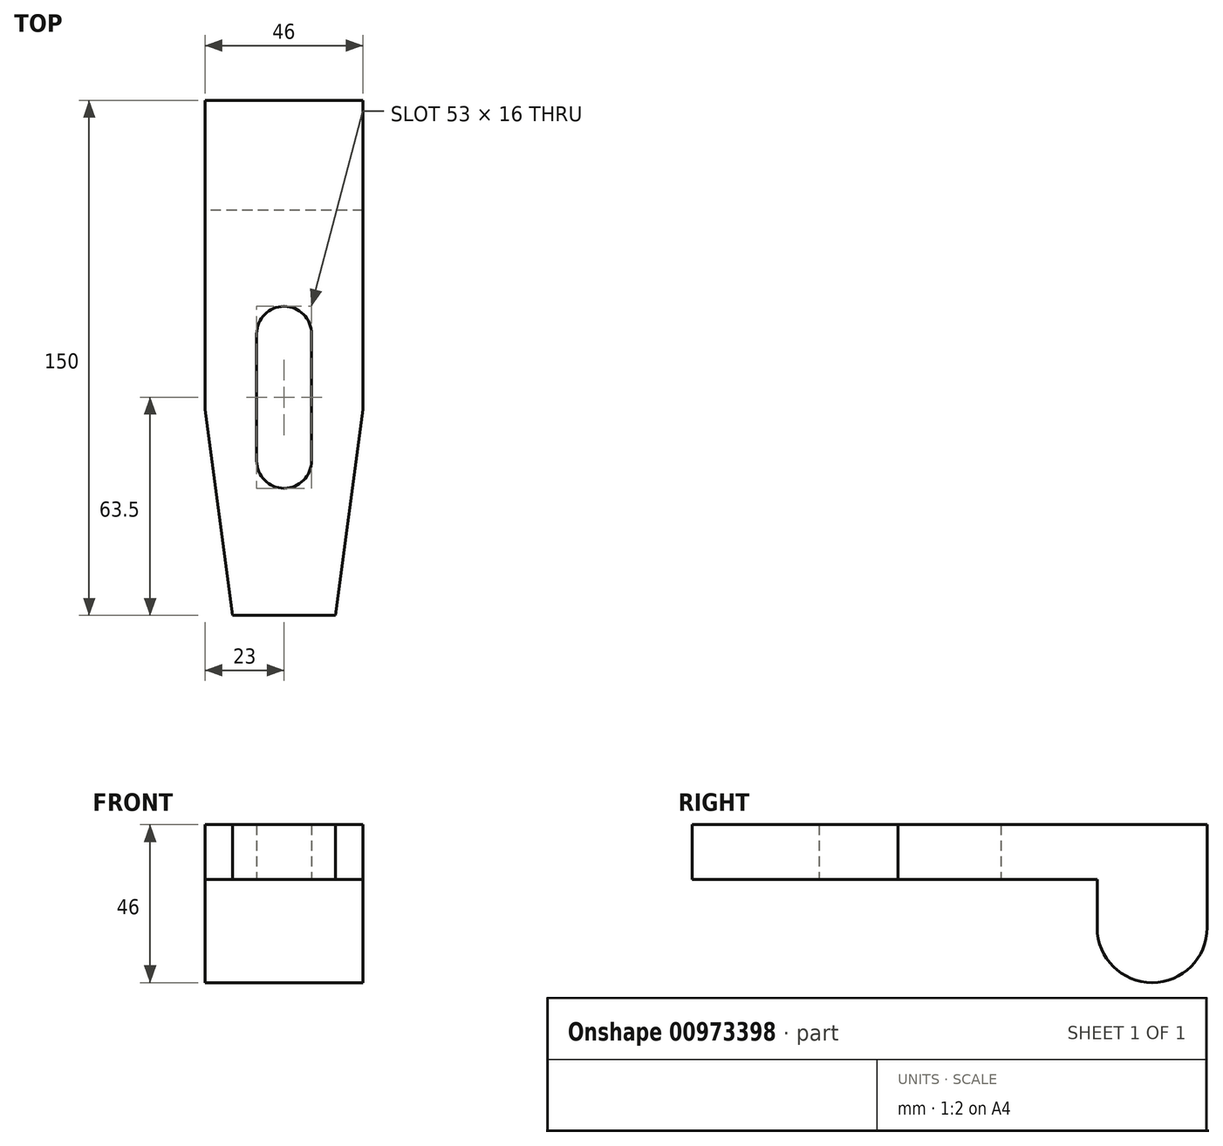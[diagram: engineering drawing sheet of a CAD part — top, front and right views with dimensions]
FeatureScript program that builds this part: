
annotation { "Feature Type Name" : "Feature", "Feature Type Description" : "" }
export const myFeature = defineFeature(function(context is Context, id is Id, definition is map)
    precondition{}
    {
        {
            var Q0;
            Q0=qCreatedBy(makeId("Top.planeOp"),FACE);
            var sketch = newSketch(context, id + "F0", { "sketchPlane" : qUnion([Q0])});
            skLineSegment(sketch, "E0", {"start": v(-23, 0) * mm, "end": v(-23, 68) * mm});
            skLineSegment(sketch, "E1", {"start": v(-23, 68) * mm, "end": v(23, 68) * mm});
            skLineSegment(sketch, "E2", {"start": v(23, 68) * mm, "end": v(23, 0) * mm});
            skLineSegment(sketch, "E3", {"start": v(-23, 0) * mm, "end": v(-23, -22) * mm});
            skLineSegment(sketch, "E4", {"start": v(23, -22) * mm, "end": v(23, 0) * mm});
            skLineSegment(sketch, "E5", {"start": v(0, -82) * mm, "end": v(-15, -82) * mm});
            skLineSegment(sketch, "E6", {"start": v(-15, -82) * mm, "end": v(0, -82) * mm});
            skLineSegment(sketch, "E7", {"start": v(0, -82) * mm, "end": v(15, -82) * mm});
            skLineSegment(sketch, "E8", {"start": v(15, -82) * mm, "end": v(23, -22) * mm});
            skLineSegment(sketch, "E9", {"start": v(-23, -22) * mm, "end": v(-15, -82) * mm});
            skLineSegment(sketch, "E10.right", {"start": v(-8, 0) * mm, "end": v(-8, -37) * mm});
            skLineSegment(sketch, "E11.right", {"start": v(8, 0) * mm, "end": v(8, -37) * mm});
            skArc(sketch, "E12", {"start": v(-8, -37) * mm, "mid": v(0, -45) * mm, "end": v(8, -37) * mm});
            skArc(sketch, "E13", {"start": v(8, 0) * mm, "mid": v(0, 8) * mm, "end": v(-8, 0) * mm});
            skSolve(sketch);
        }
        {
            var Q0;
            Q0=makeQuery(id+"F0.imprint","IMPRINT",FACE,{"disambiguationData":[TD([[makeQuery(id+"F0.imprint","IMPRINT",EDGE,{"derivedFrom":sQuery(id+"F0.wireOp",EDGE,"E0")}),-1.0]])]});
            extrude(context, id + "F1", {"entities" : qUnion([Q0]), "depth" : 16 * mm, "offsetDistance" : 25 * mm});
        }
        {
            var Q0;
            Q0=qCreatedBy(makeId("Right.planeOp"),FACE);
            var sketch = newSketch(context, id + "F2", { "sketchPlane" : qUnion([Q0])});
            skLineSegment(sketch, "E14", {"start": v(36, 0) * mm, "end": v(44.25, 0) * mm});
            skLineSegment(sketch, "E15", {"start": v(68, 0) * mm, "end": v(68, -14) * mm});
            skLineSegment(sketch, "E16", {"start": v(36, -14) * mm, "end": v(36, 0) * mm});
            skArc(sketch, "E17", {"start": v(36, -14) * mm, "mid": v(52, -30) * mm, "end": v(68, -14) * mm});
            skLineSegment(sketch, "E18.trimOffspring", {"start": v(59.75, 0) * mm, "end": v(68, 0) * mm});
            skLineSegment(sketch, "E19", {"start": v(59.75, 0) * mm, "end": v(44.25, 0) * mm});
            skSolve(sketch);
        }
        {
            var Q0;
            Q0=makeQuery(id+"F2.imprint","IMPRINT",FACE,{"disambiguationData":[TD([[makeQuery(id+"F2.imprint","IMPRINT",EDGE,{"derivedFrom":sQuery(id+"F2.wireOp",EDGE,"E14")}),-1.0]])]});
            extrude(context, id + "F3", {"entities" : qUnion([Q0]), "operationType" : NewBodyOperationType.ADD, "depth" : 23 * mm, "offsetDistance" : 25 * mm, "hasSecondDirection" : true, "secondDirectionOppositeDirection" : true, "secondDirectionDepth" : 23 * mm});
        }
    });
